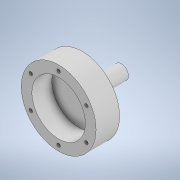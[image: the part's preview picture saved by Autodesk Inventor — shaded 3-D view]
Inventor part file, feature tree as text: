
AUTODESK INVENTOR PART (.ipt)
format: ipt  version: 2020 (Build 240168000, 168)  size: 1,588,224 bytes
history: native  units: mm
features: other x8, reference x6, sketch x5, extrude x5, hole x2, projected_geometry x2
ambient origin geometry x8: Origin, YZ Plane, XZ Plane, XY Plane, X Axis, Y Axis, Z Axis, Center Point
bodies: Body1 (feature_tree)
feature tree (28):
  other  "솔리드1"
  other  "작업 평면3"
  sketch  "스케치2"
  extrude  "돌출5"  Depth=20.0mm
  other  "작업 평면4"
  extrude  "돌출8"  Depth=20.0mm TaperAngle=0.0deg
  extrude  "돌출9"  Depth=20.0mm
  extrude  "돌출10"  Depth=35.0mm TaperAngle=0.0deg
  sketch  "스케치9"
  other  "작업 평면5"
  hole  "구멍2"  [1 undecoded]
  extrude  "돌출14"  Depth=5.0mm TaperAngle=0.0deg
  hole  "구멍3"  [1 undecoded]
  reference  "참조5"
  reference  "참조6"
  reference  "참조7"
  reference  "참조8"
  reference  "참조9"
  reference  "참조10"
  sketch  "스케치6"
  sketch  "스케치7"
  projected_geometry  "투영된 루프4"
  projected_geometry  "투영된 루프6"
  sketch  "스케치12"
  other  "<userpath>\Documents\Inventor\CoMoVi\조립품1.iam"
  other  "조립품1.iam"
  other  "Motor:1"
  other  "Motor_key:1"
note: 2 required parameter values undecoded (feature->parameter linkage not recoverable at this tier; creation-order binding heuristic only, values carry confidence <= 0.55)
